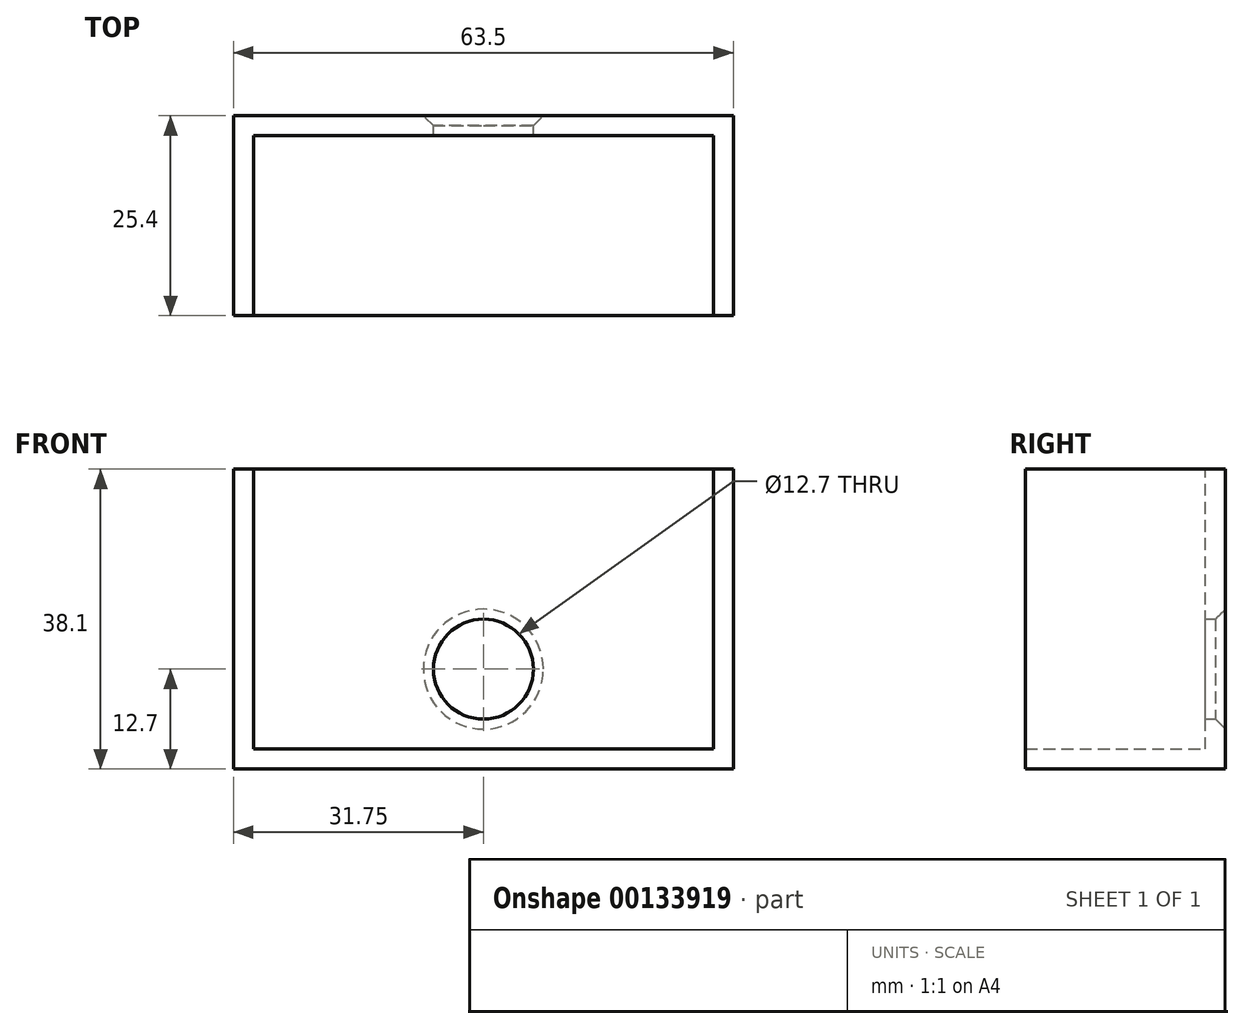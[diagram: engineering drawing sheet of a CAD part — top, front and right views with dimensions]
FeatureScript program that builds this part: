
annotation { "Feature Type Name" : "Feature", "Feature Type Description" : "" }
export const myFeature = defineFeature(function(context is Context, id is Id, definition is map)
    precondition{}
    {
        {
            var Q0;
            Q0=qCreatedBy(makeId("Front.planeOp"),FACE);
            var sketch = newSketch(context, id + "F0", { "sketchPlane" : qUnion([Q0])});
            skLineSegment(sketch, "E0.bottom", {"start": v(0, 0) * mm, "end": v(63.5, 0) * mm});
            skLineSegment(sketch, "E0.top", {"start": v(0, 38.1) * mm, "end": v(63.5, 38.1) * mm});
            skLineSegment(sketch, "E0.left", {"start": v(0, 0) * mm, "end": v(0, 38.1) * mm});
            skLineSegment(sketch, "E0.right", {"start": v(63.5, 0) * mm, "end": v(63.5, 38.1) * mm});
            skSolve(sketch);
        }
        {
            var Q0;
            Q0=makeQuery(id+"F0.imprint","IMPRINT",FACE,{"disambiguationData":[TD([[makeQuery(id+"F0.imprint","IMPRINT",EDGE,{"derivedFrom":sQuery(id+"F0.wireOp",EDGE,"E0.bottom")}),1.0]])]});
            extrude(context, id + "F1", {"entities" : qUnion([Q0]), "depth" : 25.4 * mm});
        }
        {
            var Q0;
            Q0=makeQuery(id+"F1.opExtrude","CAP_FACE",FACE,{"disambiguationData":[OSD([sQuery(id+"F0.wireOp",EDGE,"E0.bottom"),sQuery(id+"F0.wireOp",EDGE,"E0.top"),sQuery(id+"F0.wireOp",EDGE,"E0.left"),sQuery(id+"F0.wireOp",EDGE,"E0.right")])],"isStart":false});
            var Q1;
            Q1=makeQuery(id+"F1.opExtrude","SWEPT_FACE",FACE,{"disambiguationData":[OSD([sQuery(id+"F0.wireOp",EDGE,"E0.top")])]});
            shell(context, id + "F2", {"entities" : qUnion([Q0, Q1]), "thickness" : 2.54 * mm});
        }
        {
            var Q0;
            Q0=makeQuery(id+"F1.opExtrude","CAP_FACE",FACE,{"disambiguationData":[OSD([sQuery(id+"F0.wireOp",EDGE,"E0.bottom"),sQuery(id+"F0.wireOp",EDGE,"E0.top"),sQuery(id+"F0.wireOp",EDGE,"E0.left"),sQuery(id+"F0.wireOp",EDGE,"E0.right")])],"isStart":true});
            var sketch = newSketch(context, id + "F3", { "sketchPlane" : qUnion([Q0])});
            skPoint(sketch, "E1", {"position": v(-31.75, 12.7) * mm});
            skSolve(sketch);
        }
        {
            var Q0;
            Q0=sQuery(id+"F3.wireOp",VERTEX,"E1");
            var Q1;
            Q1=makeQuery(id+"F1.opExtrude","SWEPT_BODY",BODY,{"disambiguationData":[OSD([sQuery(id+"F0.wireOp",EDGE,"E0.bottom"),sQuery(id+"F0.wireOp",EDGE,"E0.top"),sQuery(id+"F0.wireOp",EDGE,"E0.left"),sQuery(id+"F0.wireOp",EDGE,"E0.right")])]});
            hole(context, id + "F4", {"style" : HoleStyle.C_SINK, "endStyle" : HoleEndStyle.THROUGH, "holeDiameter" : 12.7 * mm, "cSinkDiameter" : 15.24 * mm, "cSinkAngle" : 90 * degree, "locations" : qUnion([Q0]), "scope" : qUnion([Q1]), "isTappedThrough" : true});
        }
    });
